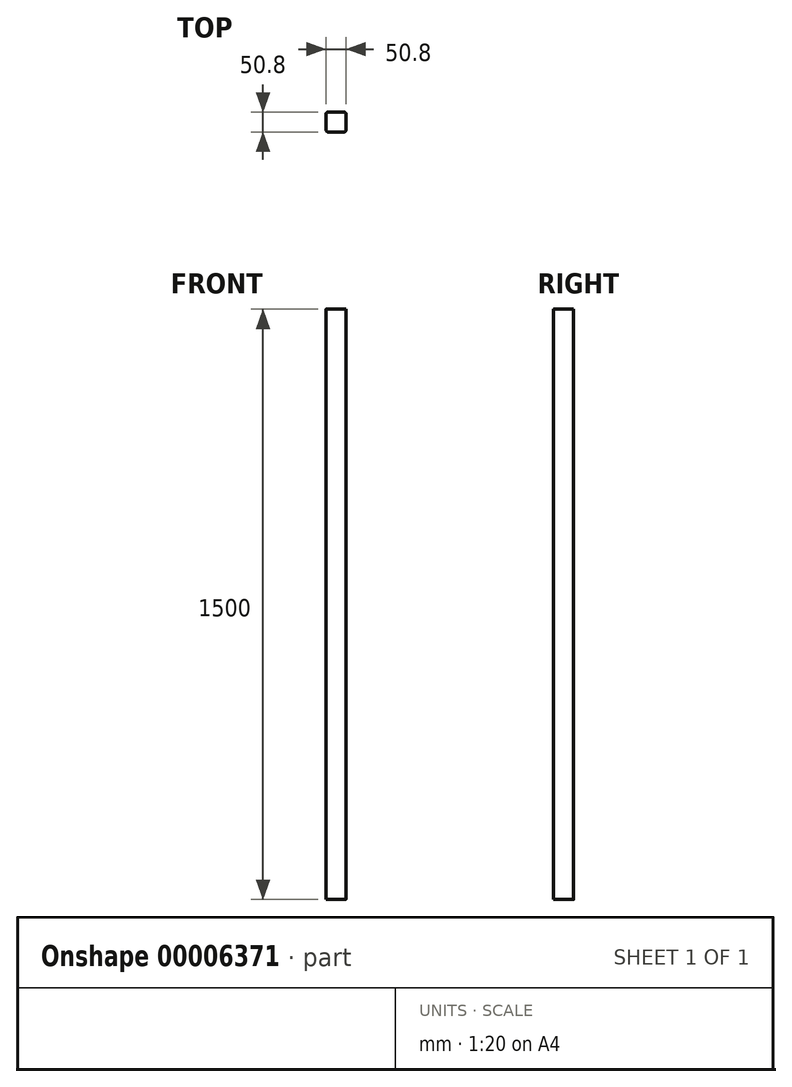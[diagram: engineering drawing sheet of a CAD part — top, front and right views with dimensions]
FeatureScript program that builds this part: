
annotation { "Feature Type Name" : "Feature", "Feature Type Description" : "" }
export const myFeature = defineFeature(function(context is Context, id is Id, definition is map)
    precondition{}
    {
        {
            var Q0;
            Q0=qCreatedBy(makeId("Top.planeOp"),FACE);
            var sketch = newSketch(context, id + "F0", { "sketchPlane" : qUnion([Q0])});
            skLineSegment(sketch, "E0.rect.bottom", {"start": v(20.4, -25.4) * mm, "end": v(-19.4, -25.4) * mm});
            skLineSegment(sketch, "E0.rect.top", {"start": v(20.4, 25.4) * mm, "end": v(-20.4, 25.4) * mm});
            skLineSegment(sketch, "E0.rect.left", {"start": v(25.4, -20.4) * mm, "end": v(25.4, 20.4) * mm});
            skLineSegment(sketch, "E0.rect.right", {"start": v(-25.4, -19.4) * mm, "end": v(-25.4, 20.4) * mm});
            skPoint(sketch, "E0.rect.middle", {"position": v(0, 0) * mm});
            skPoint(sketch, "E1.visualSharp", {"position": v(25.4, -25.4) * mm});
            skArc(sketch, "E1.filletArc", {"start": v(20.4, -25.4) * mm, "mid": v(23.94, -23.94) * mm, "end": v(25.4, -20.4) * mm});
            skPoint(sketch, "E2.visualSharp", {"position": v(25.4, 25.4) * mm});
            skArc(sketch, "E2.filletArc", {"start": v(25.4, 20.4) * mm, "mid": v(23.94, 23.94) * mm, "end": v(20.4, 25.4) * mm});
            skPoint(sketch, "E3.visualSharp", {"position": v(-25.4, 25.4) * mm});
            skArc(sketch, "E3.filletArc", {"start": v(-20.4, 25.4) * mm, "mid": v(-23.94, 23.94) * mm, "end": v(-25.4, 20.4) * mm});
            skPoint(sketch, "E4.visualSharp", {"position": v(-25.4, -25.4) * mm});
            skArc(sketch, "E4.filletArc", {"start": v(-25.4, -19.4) * mm, "mid": v(-23.64, -23.64) * mm, "end": v(-19.4, -25.4) * mm});
            skSolve(sketch);
        }
        {
            var Q0;
            Q0=makeQuery(id+"F0.imprint","IMPRINT",FACE,{"disambiguationData":[TD([[makeQuery(id+"F0.imprint","IMPRINT",EDGE,{"derivedFrom":sQuery(id+"F0.wireOp",EDGE,"E0.rect.bottom")}),-1.0]])]});
            extrude(context, id + "F1", {"entities" : qUnion([Q0]), "depth" : 1500 * mm});
        }
    });
